# Revit family: EBS4LEDS-xx-xx-xx_V1.0_Non-Hosted_R16
name_source: partatom
category: Lighting Fixtures
revit_build: Autodesk Revit 2016 (Build: 20151007_0715(x64)
units: mm (PartAtom-declared; Revit-internal decimal feet)

## family parameters
Always vertical = Yes
Cut with Voids When Loaded = No
Light Source = Yes
OmniClass Number = 23.80.70.00
OmniClass Title = Lighting
Part Type = Normal
Room Calculation Point = No
Round Connector Dimension = Use Diameter
Shared = No
Work Plane-Based = No

## types (4) — shared parameters
AS2293 Classification = C0=D50 C90=D16
Battery = 3.2V 3000mAh
Battery Type = Lithium Iron Phosphate,
Charging Method = Intelligent current limited constant voltage
Color Filter = 16777215
Construction = Powder coated steel body and PC/ABS end cap
Diffuser = Acrylic prismatic diffuser
Dimming Lamp Color Temperature Shift = <None>
Emergency Lumen Output = 347.5lm
Emit Shape Visible in Rendering = No
Emit from Rectangle Length = 1219 mm
Emit from Rectangle Width = 610 mm
IP Rating = IP20
Manufacturer = Clevertronics
Mounting = Surface mount
Operating Mode = Sustained
Operating Temperature = 0˚C to 40˚C
Operating Voltage = 240V AC; 50Hz
Photometric Web File = LL22482_EBS4LEDS-DIF-LI_AUB03510010001(AS2293.3,Classification).ies
Power Factor = 0.95
Replacement Battery = 1560156 BATT:LiFePO4 3.2V 3.0Ah 200mm lead, BRKT
Replacement lamp = 8002695 PCA:LED Strip 8S6P, ALS-13-840-0-02-B
Testing System = Manual test switch
Tilt Angle = 90.00°

## per-type parameters (varying)
| type | Description | Dimensions (L x W x H) | LED Driver | Lamp | MIC Number | Power Consumption | Power Consumption (Standby) | Product Description | Replacement Driver | Replacement Emergency Driver | Replacement Item | Total Lumen Output | Type Comments | Weight |
| EBS4LEDS-DIF-LI | Economy Lithium 4ft Odyssey Quantum LED diffused batten | 1238mm x 120mm x 110mm | 50W 700mA, XZ-STB50, 50,000hr | LED strip module, 4,000K natural white, 50,000h life [L70/B50 Ta 40°C], Ra>80 | AUB03510010001 | 37 Watts (Lamps ON), | 0.4 Watts (Lamps OFF) | Economy Lithium 4ft Odyssey Quantum LED diffused batten | 1330059 LED XZ Driver - 50w 700mA, 30-54V | ELIFE-X-LI-CKIT-2LEDSL-NP  Lifelight, Control Only,2LED,3.0Ah,325mA |  | 4585 lm @ 123lm/W | Economy Lithium 4ft Odyssey Quantum LED diffused batten |  |
| EBS4LEDS-DIF-MS-HL-LI | Economy Lithium 4ft Odyssey Quantum LED diffused batten with Hi/Lo Microwave Sensor
Control of the Lamps (10%-100%) | 1238mm x 120mm x 110mm | 55w, 500-1200mA, 12-50V | LED strip module, 4,000K natural white, 50,000h life [L70/B50 Ta 40°C], Ra>80 | AUB03510090001 | 37 Watts (Lamps ON), | 0.4 Watts (Lamps OFF) | Economy Lithium 4ft Odyssey Quantum LED diffused batten with Hi/Lo Microwave Sensor
Control of the Lamps (10%-100%) | 1330070 HL Driver - 55w, 500-1200mA, 12-50V | ELIFE-X-LI-CKIT-2LEDSL-NP Lifelight, Control Only,2LED,3.0Ah,325mA | 1190118 Sensor: Microwave motion, IP20, MC049V | 4585 lm @ 123lm/W | Economy Lithium 4ft Odyssey Quantum LED diffused batten with Hi/Lo Microwave Sensor
Control of the Lamps (10%-100%) |  |
| EBS4LEDS-LO-DIF-LI | Economy Lithium Odyssey Quantum 1200mm LED Diffused Batten
Control of the Lamps (10%-100%) | 1238mm x 120mm x 108mm | LED Driver – 21W, 700mA, 220-240V | LED Strip Module, 4,000K Natural White, 50,000h Life [L70/B50 Ta 40°C], Ra>80 | AUB03510040001 | 19W (Lamps ON) | 0.4W (Lamps OFF, Standby) | Economy Lithium Odyssey Quantum 1200mm LED Diffused Batten | 1330023 LED Driver – 21W, 700mA, 220-240V | ELIFE-X-LI-CKIT-2LEDSL-NP Lifelight, Control Only,2LED,3.0Ah,325mA |  | 2437lm @ 128lm/W | Economy Lithium Odyssey Quantum 1200mm LED Diffused Batten | 3.3 kg |
| EBS4LEDS-LO-DIF-MS-HL-LI | Economy Lithium Odyssey Quantum 1200mm LED Diffused Batten with Hi/Lo Microwave
Sensor Control of the Lamps (10%-100%)
Control of the Lamps (10%-100%) | 1238mm x 120mm x 108mm | HL Driver – 55W, 500-1200mA, 12-50V | LED Strip Module, 4,000K Natural White, 50,000h Life [L70/B50 Ta 40°C], Ra>80 | AUB03510100001 | 20W (Lamps ON) | 0.4W (Lamps OFF, Standby) | Economy Lithium Odyssey Quantum 1200mm LED Diffused Batten with Hi/Lo Microwave
Sensor Control of the Lamps (10%-100%) | 1330070 HL Driver – 55W, 500-1200mA, 12-50V | ELIFE-X-LI-CKIT-2LEDSL-NP Lifelight, Control Only,2LED,3.0Ah,325mA | 1190118 SENSOR: Microwave Motion IP20, MC049V | 2437lm @ 120lm/W | Economy Lithium Odyssey Quantum 1200mm LED Diffused Batten with Hi/Lo Microwave
Sensor Control of the Lamps (10%-100%) | 3.3 kg |

note: column(s) folded — value = type name in every type: Model

## geometry (parser evidence)
native form markers: Sweep x2
no freeform markers — native parametric forms only
